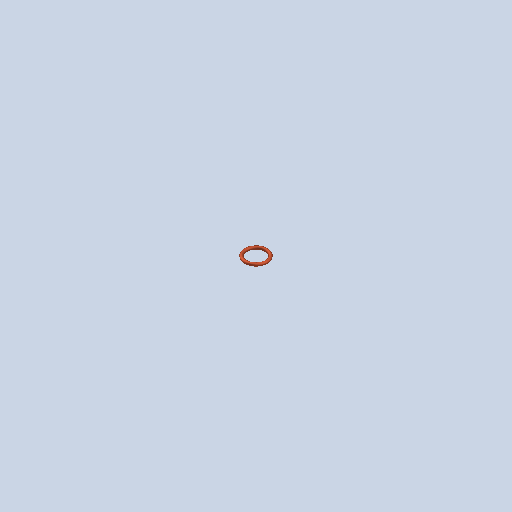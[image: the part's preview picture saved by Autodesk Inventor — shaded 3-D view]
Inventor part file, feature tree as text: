
AUTODESK INVENTOR PART (.ipt)
format: ipt  version: 2024 (Build 280153000, 153)  size: 248,832 bytes
history: native  units: in
note: dims shown in document units (in); Inventor stores cm internally (conversion verified against a paired STEP export)
features: revolve x1, direct_edit x1, sketch x1, other x1
ambient origin geometry x8: Origin, YZ Plane, XZ Plane, XY Plane, X Axis, Y Axis, Z Axis, Center Point
bodies: Solid1 (feature_tree)
feature tree (4):
  revolve  "Revolution1"  [1 undecoded]
  direct_edit  "Direct Edit1"
  sketch  "Sketch1"  dims[d0=0.2117in d1=0.0625in d2=90.0deg d3=3.937in d4=0.3937in d5=0.3937in]
  other  "Scale1"
note: 1 required parameter value undecoded (feature->parameter linkage not recoverable at this tier; creation-order binding heuristic only, values carry confidence <= 0.55)
